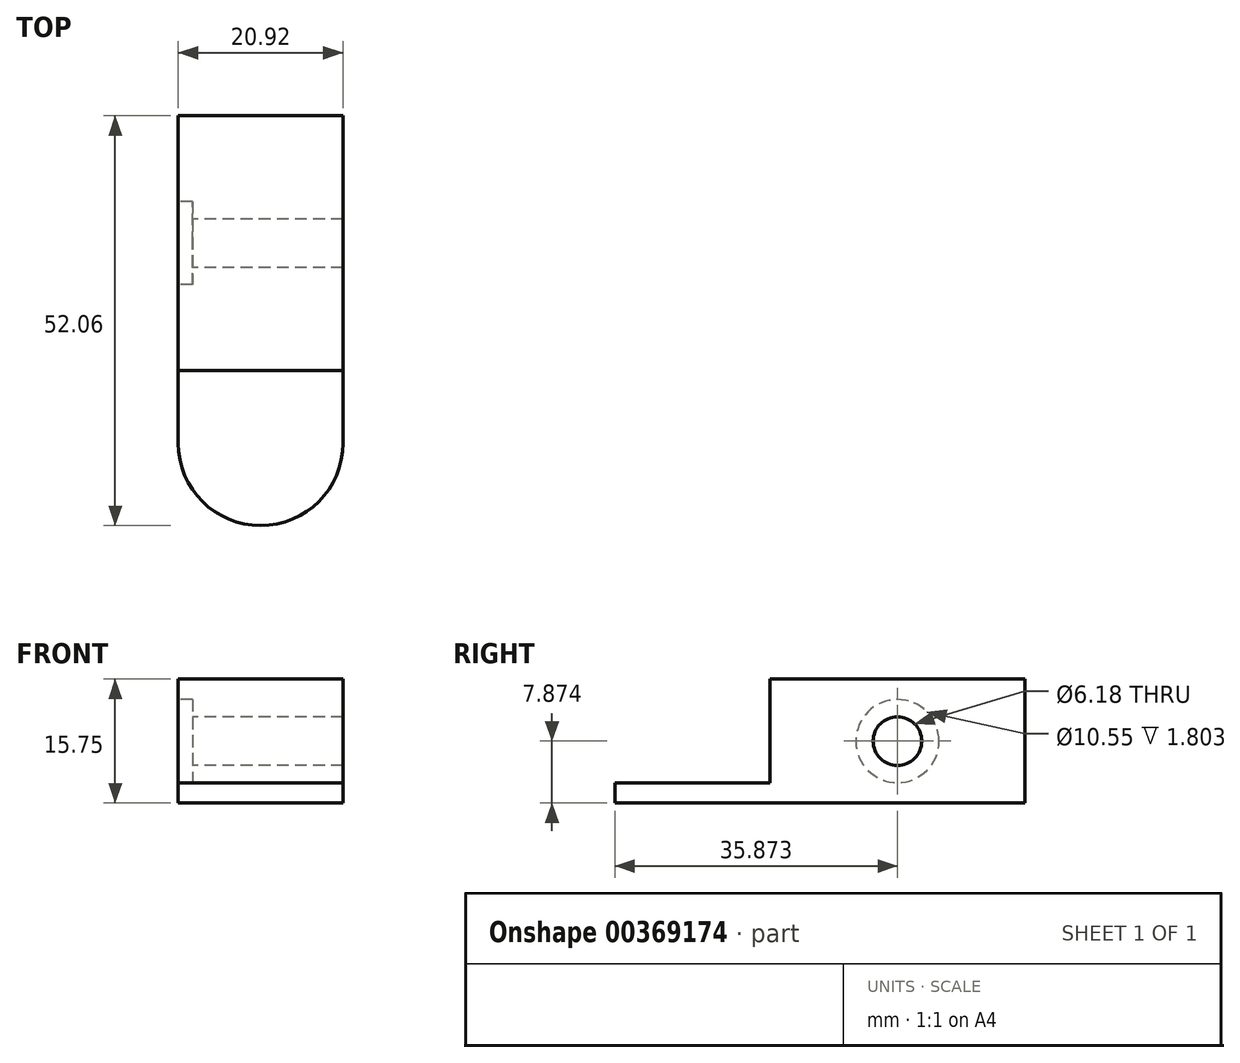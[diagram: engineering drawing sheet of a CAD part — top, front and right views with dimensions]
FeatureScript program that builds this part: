
annotation { "Feature Type Name" : "Feature", "Feature Type Description" : "" }
export const myFeature = defineFeature(function(context is Context, id is Id, definition is map)
    precondition{}
    {
        {
            var Q0;
            Q0=qCreatedBy(makeId("Top.planeOp"),FACE);
            var sketch = newSketch(context, id + "F0", { "sketchPlane" : qUnion([Q0])});
            skLineSegment(sketch, "E0.bottom", {"start": v(10.46, 20.8) * mm, "end": v(-10.46, 20.8) * mm});
            skLineSegment(sketch, "E0.top", {"start": v(10.46, -20.8) * mm, "end": v(-10.46, -20.8) * mm});
            skLineSegment(sketch, "E0.left", {"start": v(10.46, 20.8) * mm, "end": v(10.46, -20.8) * mm});
            skLineSegment(sketch, "E0.right", {"start": v(-10.46, 20.8) * mm, "end": v(-10.46, -20.8) * mm});
            skPoint(sketch, "E0.middle", {"position": v(0, 0) * mm});
            skArc(sketch, "E1", {"start": v(-10.46, -20.8) * mm, "mid": v(0, -31.26) * mm, "end": v(10.46, -20.8) * mm});
            skLineSegment(sketch, "E2", {"start": v(-10.46, -11.58) * mm, "end": v(10.46, -11.58) * mm});
            skSolve(sketch);
        }
        {
            var Q0;
            Q0=makeQuery(id+"F0.imprint","IMPRINT",FACE,{"disambiguationData":[TD([[makeQuery(id+"F0.imprint","IMPRINT",EDGE,{"derivedFrom":sQuery(id+"F0.wireOp",EDGE,"E0.top")}),1.0]])]});
            var Q1;
            {var subQ0=sQuery(id+"F0.wireOp",EDGE,"E0.top");Q1=makeQuery(id+"F0.imprint","IMPRINT",FACE,{"disambiguationData":[TD([[makeQuery(id+"F0.imprint","IMPRINT",EDGE,{"derivedFrom":subQ0}),-1.0]])]});}
            extrude(context, id + "F1", {"entities" : qUnion([Q0, Q1]), "depth" : 2.54 * mm});
        }
        {
            var Q0;
            {var subQ0=sQuery(id+"F0.wireOp",EDGE,"E0.bottom");Q0=makeQuery(id+"F0.imprint","IMPRINT",FACE,{"disambiguationData":[TD([[makeQuery(id+"F0.imprint","IMPRINT",EDGE,{"derivedFrom":subQ0}),1.0]])]});}
            extrude(context, id + "F2", {"entities" : qUnion([Q0]), "operationType" : NewBodyOperationType.ADD, "depth" : 15.75 * mm});
        }
        {
            var Q0;
            {var subQ0=sQuery(id+"F0.wireOp",EDGE,"E0.right");Q0=makeQuery(id+"F2.boolean.opBoolean","MERGE",FACE,{"derivedFrom":[makeQuery(id+"F1.opExtrude","SWEPT_FACE",FACE,{"disambiguationData":[OSD([subQ0])]}),makeQuery(id+"F2.opExtrude","SWEPT_FACE",FACE,{"disambiguationData":[OSD([subQ0])]})]});}
            var sketch = newSketch(context, id + "F3", { "sketchPlane" : qUnion([Q0])});
            skLineSegment(sketch, "E3", {"start": v(-4.61, 15.75) * mm, "end": v(-4.61, 0) * mm});
            skLineSegment(sketch, "E4", {"start": v(-20.8, 7.87) * mm, "end": v(11.58, 7.87) * mm});
            skCircle(sketch, "E5", {"center": v(-4.61, 7.87) * mm, "radius": 5.28 * mm});
            skCircle(sketch, "E6", {"center": v(-4.61, 7.87) * mm, "radius": 3.1 * mm});
            skSolve(sketch);
        }
        {
            var Q0;
            {var subQ0=sQuery(id+"F3.wireOp",EDGE,"E4");var subQ1=sQuery(id+"F3.wireOp",EDGE,"E3");var subQ2=makeQuery(id+"F3.imprint","INTERSECT",VERTEX,{"derivedFrom":[subQ1,subQ0]});Q0=makeQuery(id+"F3.imprint","IMPRINT",FACE,{"disambiguationData":[TD([[makeQuery(id+"F3.imprint","IMPRINT",EDGE,{"disambiguationData":[TD([[subQ2,-1.0]])],"derivedFrom":subQ1}),-1.0]])]});}
            var Q1;
            {var subQ0=sQuery(id+"F3.wireOp",EDGE,"E4");var subQ1=sQuery(id+"F3.wireOp",EDGE,"E3");var subQ2=makeQuery(id+"F3.imprint","INTERSECT",VERTEX,{"derivedFrom":[subQ1,subQ0]});Q1=makeQuery(id+"F3.imprint","IMPRINT",FACE,{"disambiguationData":[TD([[makeQuery(id+"F3.imprint","IMPRINT",EDGE,{"disambiguationData":[TD([[subQ2,-1.0]])],"derivedFrom":subQ1}),1.0]])]});}
            var Q2;
            {var subQ0=sQuery(id+"F3.wireOp",EDGE,"E6");var subQ1=sQuery(id+"F3.wireOp",EDGE,"E3");var subQ2=makeQuery(id+"F3.imprint","INTERSECT",VERTEX,{"disambiguationData":[OD(0.0)],"derivedFrom":[subQ1,subQ0]});Q2=makeQuery(id+"F3.imprint","IMPRINT",FACE,{"disambiguationData":[TD([[makeQuery(id+"F3.imprint","IMPRINT",EDGE,{"disambiguationData":[TD([[subQ2,-1.0]])],"derivedFrom":subQ1}),1.0]])]});}
            var Q3;
            {var subQ0=sQuery(id+"F3.wireOp",EDGE,"E6");var subQ1=sQuery(id+"F3.wireOp",EDGE,"E3");var subQ2=makeQuery(id+"F3.imprint","INTERSECT",VERTEX,{"disambiguationData":[OD(0.0)],"derivedFrom":[subQ1,subQ0]});Q3=makeQuery(id+"F3.imprint","IMPRINT",FACE,{"disambiguationData":[TD([[makeQuery(id+"F3.imprint","IMPRINT",EDGE,{"disambiguationData":[TD([[subQ2,-1.0]])],"derivedFrom":subQ1}),-1.0]])]});}
            extrude(context, id + "F4", {"entities" : qUnion([Q0, Q1, Q2, Q3]), "operationType" : NewBodyOperationType.REMOVE, "oppositeDirection" : true, "depth" : 25.4 * mm});
        }
        {
            var Q0;
            {var subQ0=sQuery(id+"F3.wireOp",EDGE,"E5");var subQ1=sQuery(id+"F3.wireOp",EDGE,"E3");var subQ2=makeQuery(id+"F3.imprint","INTERSECT",VERTEX,{"disambiguationData":[OD(0.0)],"derivedFrom":[subQ1,subQ0]});Q0=makeQuery(id+"F3.imprint","IMPRINT",FACE,{"disambiguationData":[TD([[makeQuery(id+"F3.imprint","IMPRINT",EDGE,{"disambiguationData":[TD([[subQ2,-1.0]])],"derivedFrom":subQ1}),-1.0]])]});}
            var Q1;
            {var subQ0=sQuery(id+"F3.wireOp",EDGE,"E5");var subQ1=sQuery(id+"F3.wireOp",EDGE,"E3");var subQ2=makeQuery(id+"F3.imprint","INTERSECT",VERTEX,{"disambiguationData":[OD(0.0)],"derivedFrom":[subQ1,subQ0]});Q1=makeQuery(id+"F3.imprint","IMPRINT",FACE,{"disambiguationData":[TD([[makeQuery(id+"F3.imprint","IMPRINT",EDGE,{"disambiguationData":[TD([[subQ2,-1.0]])],"derivedFrom":subQ1}),1.0]])]});}
            var Q2;
            {var subQ0=sQuery(id+"F3.wireOp",EDGE,"E6");var subQ1=sQuery(id+"F3.wireOp",EDGE,"E3");var subQ2=makeQuery(id+"F3.imprint","INTERSECT",VERTEX,{"disambiguationData":[OD(1.0)],"derivedFrom":[subQ1,subQ0]});Q2=makeQuery(id+"F3.imprint","IMPRINT",FACE,{"disambiguationData":[TD([[makeQuery(id+"F3.imprint","IMPRINT",EDGE,{"disambiguationData":[TD([[subQ2,-1.0]])],"derivedFrom":subQ1}),1.0]])]});}
            var Q3;
            {var subQ0=sQuery(id+"F3.wireOp",EDGE,"E6");var subQ1=sQuery(id+"F3.wireOp",EDGE,"E3");var subQ2=makeQuery(id+"F3.imprint","INTERSECT",VERTEX,{"disambiguationData":[OD(1.0)],"derivedFrom":[subQ1,subQ0]});Q3=makeQuery(id+"F3.imprint","IMPRINT",FACE,{"disambiguationData":[TD([[makeQuery(id+"F3.imprint","IMPRINT",EDGE,{"disambiguationData":[TD([[subQ2,-1.0]])],"derivedFrom":subQ1}),-1.0]])]});}
            extrude(context, id + "F5", {"entities" : qUnion([Q0, Q1, Q2, Q3]), "operationType" : NewBodyOperationType.REMOVE, "oppositeDirection" : true, "depth" : 1.8 * mm});
        }
    });
